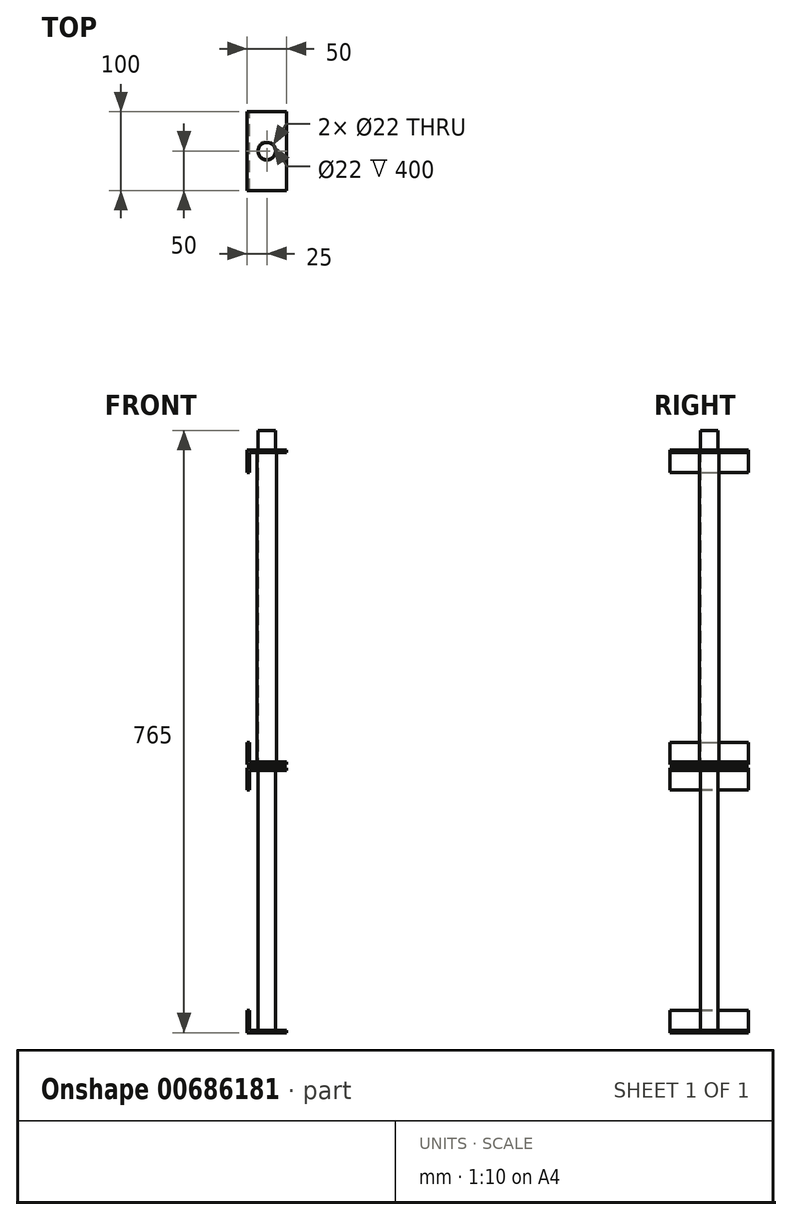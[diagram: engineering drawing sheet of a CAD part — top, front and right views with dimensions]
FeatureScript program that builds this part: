
annotation { "Feature Type Name" : "Feature", "Feature Type Description" : "" }
export const myFeature = defineFeature(function(context is Context, id is Id, definition is map)
    precondition{}
    {
        {
            var Q0;
            Q0=qCreatedBy(makeId("Right.planeOp"),FACE);
            var sketch = newSketch(context, id + "F0", { "sketchPlane" : qUnion([Q0])});
            skLineSegment(sketch, "E0.bottom", {"start": v(0, 0) * mm, "end": v(100, 0) * mm});
            skLineSegment(sketch, "E0.top", {"start": v(0, 25) * mm, "end": v(100, 25) * mm});
            skLineSegment(sketch, "E0.left", {"start": v(0, 0) * mm, "end": v(0, 25) * mm});
            skLineSegment(sketch, "E0.right", {"start": v(100, 0) * mm, "end": v(100, 25) * mm});
            skSolve(sketch);
        }
        {
            var Q0;
            Q0=makeQuery(id+"F0.imprint","IMPRINT",FACE,{"disambiguationData":[TD([[makeQuery(id+"F0.imprint","IMPRINT",EDGE,{"derivedFrom":sQuery(id+"F0.wireOp",EDGE,"E0.bottom")}),1.0]])]});
            extrude(context, id + "F1", {"entities" : qUnion([Q0]), "depth" : 3.2 * mm, "offsetDistance" : 25 * mm});
        }
        {
            var Q0;
            Q0=makeQuery(id+"F1.opExtrude","SWEPT_FACE",FACE,{"disambiguationData":[OSD([sQuery(id+"F0.wireOp",EDGE,"E0.top")])]});
            var sketch = newSketch(context, id + "F2", { "sketchPlane" : qUnion([Q0])});
            skLineSegment(sketch, "E1.bottom", {"start": v(0, 0) * mm, "end": v(50, 0) * mm});
            skLineSegment(sketch, "E1.top", {"start": v(0, 100) * mm, "end": v(50, 100) * mm});
            skLineSegment(sketch, "E1.left", {"start": v(0, 0) * mm, "end": v(0, 100) * mm});
            skLineSegment(sketch, "E1.right", {"start": v(50, 0) * mm, "end": v(50, 100) * mm});
            skSolve(sketch);
        }
        {
            var Q0;
            {var subQ2=sQuery(id+"F2.wireOp",EDGE,"E1.right");Q0=makeQuery(id+"F2.imprint","IMPRINT",FACE,{"disambiguationData":[TD([[makeQuery(id+"F2.imprint","IMPRINT",EDGE,{"derivedFrom":subQ2}),1.0]])]});}
            var Q1;
            {var subQ0=sQuery(id+"F2.wireOp",EDGE,"E1.left");Q1=makeQuery(id+"F2.imprint","IMPRINT",FACE,{"disambiguationData":[TD([[makeQuery(id+"F2.imprint","IMPRINT",EDGE,{"derivedFrom":subQ0}),-1.0]])]});}
            extrude(context, id + "F3", {"entities" : qUnion([Q0, Q1]), "operationType" : NewBodyOperationType.ADD, "depth" : 3.2 * mm, "offsetDistance" : 25 * mm});
        }
        {
            var Q0;
            Q0=makeQuery(id+"F3.opExtrude","CAP_FACE",FACE,{"disambiguationData":[OSD([sQuery(id+"F2.wireOp",EDGE,"E1.bottom"),sQuery(id+"F2.wireOp",EDGE,"E1.top"),sQuery(id+"F2.wireOp",EDGE,"E1.left"),sQuery(id+"F2.wireOp",EDGE,"E1.right")])],"isStart":false});
            var sketch = newSketch(context, id + "F4", { "sketchPlane" : qUnion([Q0])});
            skCircle(sketch, "E2", {"center": v(25, 50) * mm, "radius": 12.5 * mm});
            skPoint(sketch, "E2.centerSnap0", {"position": v(50, 50) * mm});
            skPoint(sketch, "E2.centerSnap1", {"position": v(25, 100) * mm});
            skSolve(sketch);
        }
        {
            var Q0;
            Q0=makeQuery(id+"F4.imprint","IMPRINT",FACE,{"disambiguationData":[TD([[makeQuery(id+"F4.imprint","IMPRINT",EDGE,{"derivedFrom":sQuery(id+"F4.wireOp",EDGE,"E2")}),1.0]])]});
            extrude(context, id + "F5", {"entities" : qUnion([Q0]), "oppositeDirection" : true, "depth" : 400 * mm, "offsetDistance" : 25 * mm});
        }
        {
            var Q0;
            Q0=makeQuery(id+"F5.opExtrude","SWEPT_BODY",BODY,{"disambiguationData":[OSD([sQuery(id+"F4.wireOp",EDGE,"E2")])]});
            var Q1;
            Q1=makeQuery(id+"F1.opExtrude","SWEPT_BODY",BODY,{"disambiguationData":[OSD([sQuery(id+"F0.wireOp",EDGE,"E0.bottom"),sQuery(id+"F0.wireOp",EDGE,"E0.top"),sQuery(id+"F0.wireOp",EDGE,"E0.left"),sQuery(id+"F0.wireOp",EDGE,"E0.right")])]});
            booleanBodies(context, id + "F6", {"operationType" : BooleanOperationType.SUBTRACTION, "tools" : qUnion([Q0]), "targets" : qUnion([Q1]), "keepTools" : true});
        }
        {
            var Q0;
            Q0=makeQuery(id+"F5.opExtrude","CAP_FACE",FACE,{"disambiguationData":[OSD([sQuery(id+"F4.wireOp",EDGE,"E2")])],"isStart":true});
            var Q1;
            Q1=makeQuery(id+"F5.opExtrude","CAP_FACE",FACE,{"disambiguationData":[OSD([sQuery(id+"F4.wireOp",EDGE,"E2")])],"isStart":false});
            shell(context, id + "F7", {"entities" : qUnion([Q0, Q1]), "thickness" : 1.5 * mm});
        }
        {
            var Q0;
            Q0=makeQuery(id+"F5.opExtrude","CAP_FACE",FACE,{"disambiguationData":[OSD([sQuery(id+"F4.wireOp",EDGE,"E2")])],"isStart":true});
            var sketch = newSketch(context, id + "F8", { "sketchPlane" : qUnion([Q0])});
            skCircle(sketch, "E3", {"center": v(25, 50) * mm, "radius": 11 * mm});
            skSolve(sketch);
        }
        {
            var Q0;
            Q0=makeQuery(id+"F8.imprint","IMPRINT",FACE,{"disambiguationData":[TD([[makeQuery(id+"F8.imprint","IMPRINT",EDGE,{"derivedFrom":sQuery(id+"F8.wireOp",EDGE,"E3")}),1.0]])]});
            extrude(context, id + "F9", {"entities" : qUnion([Q0]), "depth" : 25 * mm, "offsetDistance" : 25 * mm, "hasSecondDirection" : true, "secondDirectionOppositeDirection" : true, "secondDirectionDepth" : 740 * mm});
        }
        {
            var Q0;
            Q0=qCreatedBy(makeId("Top.planeOp"),FACE);
            cPlane(context, id + "F10", {"entities" : qUnion([Q0]), "cplaneType" : CPlaneType.OFFSET, "offset" : 171.5 * mm, "oppositeDirection" : true, "width" : 150 * mm, "height" : 150 * mm});
        }
        {
            var Q0;
            Q0=makeQuery(id+"F1.opExtrude","SWEPT_BODY",BODY,{"disambiguationData":[OSD([sQuery(id+"F0.wireOp",EDGE,"E0.bottom"),sQuery(id+"F0.wireOp",EDGE,"E0.top"),sQuery(id+"F0.wireOp",EDGE,"E0.left"),sQuery(id+"F0.wireOp",EDGE,"E0.right")])]});
            var Q1;
            Q1=qCreatedBy(id+"F10.planeOp",FACE);
            mirror(context, id + "F11", {"operationType" : NewBodyOperationType.ADD, "entities" : qUnion([Q0]), "mirrorPlane" : qUnion([Q1])});
        }
        {
            var Q0;
            Q0=makeQuery(id+"F9.opExtrude","CAP_FACE",FACE,{"disambiguationData":[OSD([sQuery(id+"F8.wireOp",EDGE,"E3")])],"isStart":true});
            var sketch = newSketch(context, id + "F12", { "sketchPlane" : qUnion([Q0])});
            skLineSegment(sketch, "E4.bottom", {"start": v(50, -100) * mm, "end": v(0, -100) * mm});
            skLineSegment(sketch, "E4.top", {"start": v(50, 0) * mm, "end": v(0, 0) * mm});
            skLineSegment(sketch, "E4.left", {"start": v(50, -100) * mm, "end": v(50, 0) * mm});
            skLineSegment(sketch, "E4.right", {"start": v(0, -100) * mm, "end": v(0, 0) * mm});
            skPoint(sketch, "E4.middle", {"position": v(25, -50) * mm});
            skSolve(sketch);
        }
        {
            var Q0;
            Q0=makeQuery(id+"F12.imprint","IMPRINT",FACE,{"disambiguationData":[TD([[makeQuery(id+"F12.imprint","IMPRINT",EDGE,{"derivedFrom":sQuery(id+"F12.wireOp",EDGE,"E4.bottom")}),-1.0]])]});
            extrude(context, id + "F13", {"entities" : qUnion([Q0]), "oppositeDirection" : true, "depth" : 3.2 * mm, "offsetDistance" : 25 * mm});
        }
        {
            var Q0;
            Q0=makeQuery(id+"F13.opExtrude","CAP_FACE",FACE,{"disambiguationData":[OSD([sQuery(id+"F8.wireOp",EDGE,"E3"),sQuery(id+"F12.wireOp",EDGE,"E4.bottom"),sQuery(id+"F12.wireOp",EDGE,"E4.top"),sQuery(id+"F12.wireOp",EDGE,"E4.left"),sQuery(id+"F12.wireOp",EDGE,"E4.right")])],"isStart":false});
            var sketch = newSketch(context, id + "F14", { "sketchPlane" : qUnion([Q0])});
            skLineSegment(sketch, "E5.bottom", {"start": v(0, 0) * mm, "end": v(3.2, 0) * mm});
            skLineSegment(sketch, "E5.top", {"start": v(0, 100) * mm, "end": v(3.2, 100) * mm});
            skLineSegment(sketch, "E5.left", {"start": v(0, 0) * mm, "end": v(0, 100) * mm});
            skLineSegment(sketch, "E5.right", {"start": v(3.2, 0) * mm, "end": v(3.2, 100) * mm});
            skSolve(sketch);
        }
        {
            var Q0;
            Q0=makeQuery(id+"F14.imprint","IMPRINT",FACE,{"disambiguationData":[TD([[makeQuery(id+"F14.imprint","IMPRINT",EDGE,{"derivedFrom":sQuery(id+"F14.wireOp",EDGE,"E5.bottom")}),-1.0]])]});
            extrude(context, id + "F15", {"entities" : qUnion([Q0]), "operationType" : NewBodyOperationType.ADD, "depth" : 25 * mm, "offsetDistance" : 25 * mm});
        }
        {
            var Q0;
            Q0=makeQuery(id+"F13.opExtrude","CAP_FACE",FACE,{"disambiguationData":[OSD([sQuery(id+"F8.wireOp",EDGE,"E3"),sQuery(id+"F12.wireOp",EDGE,"E4.bottom"),sQuery(id+"F12.wireOp",EDGE,"E4.top"),sQuery(id+"F12.wireOp",EDGE,"E4.left"),sQuery(id+"F12.wireOp",EDGE,"E4.right")])],"isStart":false});
            cPlane(context, id + "F16", {"entities" : qUnion([Q0]), "cplaneType" : CPlaneType.OFFSET, "offset" : 165 * mm, "width" : 150 * mm, "height" : 150 * mm});
        }
        {
            var Q0;
            Q0=makeQuery(id+"F13.opExtrude","SWEPT_BODY",BODY,{"disambiguationData":[OSD([sQuery(id+"F8.wireOp",EDGE,"E3"),sQuery(id+"F12.wireOp",EDGE,"E4.bottom"),sQuery(id+"F12.wireOp",EDGE,"E4.top"),sQuery(id+"F12.wireOp",EDGE,"E4.left"),sQuery(id+"F12.wireOp",EDGE,"E4.right")])]});
            var Q1;
            Q1=qCreatedBy(id+"F16.planeOp",FACE);
            mirror(context, id + "F17", {"entities" : qUnion([Q0]), "mirrorPlane" : qUnion([Q1])});
        }
    });
